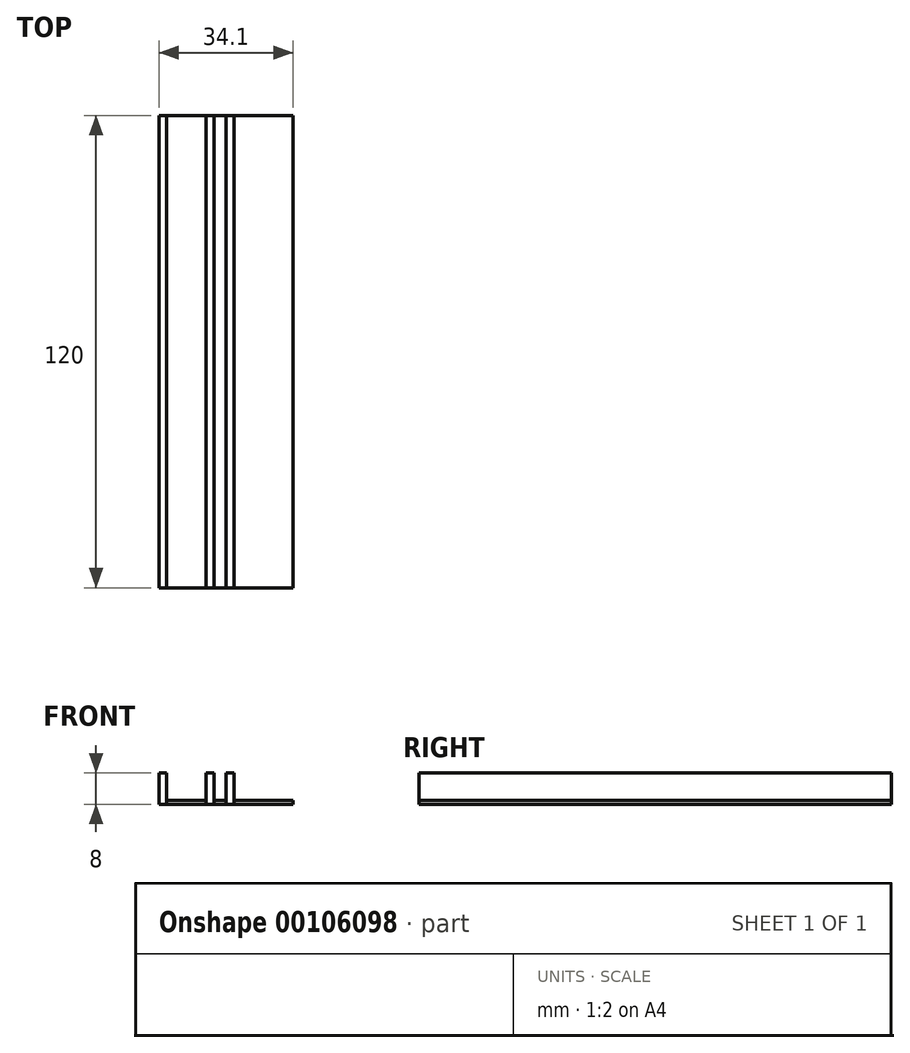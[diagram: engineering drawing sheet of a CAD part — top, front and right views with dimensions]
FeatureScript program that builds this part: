
annotation { "Feature Type Name" : "Feature", "Feature Type Description" : "" }
export const myFeature = defineFeature(function(context is Context, id is Id, definition is map)
    precondition{}
    {
        {
            var Q0;
            Q0=qCreatedBy(makeId("Top.planeOp"),FACE);
            var sketch = newSketch(context, id + "F0", { "sketchPlane" : qUnion([Q0])});
            skLineSegment(sketch, "E0.right", {"start": v(0, 44.94) * mm, "end": v(0, -75.06) * mm});
            skLineSegment(sketch, "E1", {"start": v(2, 44.94) * mm, "end": v(0, 44.94) * mm});
            skLineSegment(sketch, "E2", {"start": v(2, 44.94) * mm, "end": v(12, 44.94) * mm});
            skLineSegment(sketch, "E3.bottom", {"start": v(0, -75.06) * mm, "end": v(2, -75.06) * mm});
            skLineSegment(sketch, "E3.top", {"start": v(0, 44.94) * mm, "end": v(2, 44.94) * mm});
            skLineSegment(sketch, "E3.left", {"start": v(0, -75.06) * mm, "end": v(0, 44.94) * mm});
            skLineSegment(sketch, "E3.right", {"start": v(2, -75.06) * mm, "end": v(2, 44.94) * mm});
            skLineSegment(sketch, "E4.bottom", {"start": v(2, -75.06) * mm, "end": v(12, -75.06) * mm});
            skLineSegment(sketch, "E4.right", {"start": v(12, -75.06) * mm, "end": v(12, 44.94) * mm});
            skLineSegment(sketch, "E5", {"start": v(0, 44.94) * mm, "end": v(-3.1, 44.94) * mm});
            skLineSegment(sketch, "E6", {"start": v(-3.1, 44.94) * mm, "end": v(-5.1, 44.94) * mm});
            skLineSegment(sketch, "E7", {"start": v(-5.1, 44.94) * mm, "end": v(-20.1, 44.94) * mm});
            skLineSegment(sketch, "E8.bottom", {"start": v(-3.1, 44.94) * mm, "end": v(0, 44.94) * mm});
            skLineSegment(sketch, "E8.top", {"start": v(-3.1, -75.06) * mm, "end": v(0, -75.06) * mm});
            skLineSegment(sketch, "E8.left", {"start": v(-3.1, 44.94) * mm, "end": v(-3.1, -75.06) * mm});
            skLineSegment(sketch, "E9.bottom", {"start": v(-5.1, 44.94) * mm, "end": v(-3.1, 44.94) * mm});
            skLineSegment(sketch, "E9.top", {"start": v(-5.1, -75.06) * mm, "end": v(-3.1, -75.06) * mm});
            skLineSegment(sketch, "E9.left", {"start": v(-5.1, 44.94) * mm, "end": v(-5.1, -75.06) * mm});
            skLineSegment(sketch, "E10.bottom", {"start": v(-20.1, 44.94) * mm, "end": v(-5.1, 44.94) * mm});
            skLineSegment(sketch, "E10.top", {"start": v(-20.1, -75.06) * mm, "end": v(-5.1, -75.06) * mm});
            skLineSegment(sketch, "E10.left", {"start": v(-20.1, 44.94) * mm, "end": v(-20.1, -75.06) * mm});
            skLineSegment(sketch, "E11", {"start": v(12, 44.94) * mm, "end": v(14, 44.94) * mm});
            skLineSegment(sketch, "E12", {"start": v(14, 44.94) * mm, "end": v(14, -75.05) * mm});
            skLineSegment(sketch, "E13", {"start": v(14, -75.05) * mm, "end": v(12, -75.06) * mm});
            skLineSegment(sketch, "E14", {"start": v(14, 44.94) * mm, "end": v(17.1, 44.94) * mm});
            skLineSegment(sketch, "E15", {"start": v(17.1, 44.94) * mm, "end": v(17.1, -75.05) * mm});
            skLineSegment(sketch, "E16", {"start": v(17.1, -75.05) * mm, "end": v(14, -75.05) * mm});
            skLineSegment(sketch, "E17", {"start": v(17.1, 44.94) * mm, "end": v(19.1, 44.94) * mm});
            skLineSegment(sketch, "E18", {"start": v(19.1, 44.94) * mm, "end": v(19.1, -75.05) * mm});
            skLineSegment(sketch, "E19", {"start": v(19.1, -75.05) * mm, "end": v(17.1, -75.05) * mm});
            skLineSegment(sketch, "E20", {"start": v(19.1, 44.94) * mm, "end": v(34.1, 44.94) * mm});
            skLineSegment(sketch, "E21", {"start": v(34.1, 44.94) * mm, "end": v(34.1, -75.05) * mm});
            skLineSegment(sketch, "E22", {"start": v(34.1, -75.05) * mm, "end": v(19.1, -75.05) * mm});
            skSolve(sketch);
        }
        {
            var Q0;
            {var subQ3=sQuery(id+"F0.wireOp",EDGE,"E8.bottom");Q0=makeQuery(id+"F0.imprint","IMPRINT",FACE,{"disambiguationData":[TD([[makeQuery(id+"F0.imprint","IMPRINT",EDGE,{"derivedFrom":subQ3}),-1.0]])]});}
            var Q1;
            Q1=makeQuery(id+"F0.imprint","IMPRINT",FACE,{"disambiguationData":[TD([[makeQuery(id+"F0.imprint","IMPRINT",EDGE,{"derivedFrom":sQuery(id+"F0.wireOp",EDGE,"E4.bottom")}),1.0]])]});
            var Q2;
            Q2=makeQuery(id+"F0.imprint","IMPRINT",FACE,{"disambiguationData":[TD([[makeQuery(id+"F0.imprint","IMPRINT",EDGE,{"derivedFrom":sQuery(id+"F0.wireOp",EDGE,"E10.bottom")}),-1.0]])]});
            var Q3;
            Q3=makeQuery(id+"F0.imprint","IMPRINT",FACE,{"disambiguationData":[TD([[makeQuery(id+"F0.imprint","IMPRINT",EDGE,{"derivedFrom":sQuery(id+"F0.wireOp",EDGE,"E18")}),1.0]])]});
            var Q4;
            Q4=makeQuery(id+"F0.imprint","IMPRINT",FACE,{"disambiguationData":[TD([[makeQuery(id+"F0.imprint","IMPRINT",EDGE,{"derivedFrom":sQuery(id+"F0.wireOp",EDGE,"E12")}),1.0]])]});
            extrude(context, id + "F1", {"entities" : qUnion([Q0, Q1, Q2, Q3, Q4]), "depth" : 1 * mm});
        }
        {
            var Q0;
            Q0=makeQuery(id+"F0.imprint","IMPRINT",FACE,{"disambiguationData":[TD([[makeQuery(id+"F0.imprint","IMPRINT",EDGE,{"derivedFrom":sQuery(id+"F0.wireOp",EDGE,"E9.bottom")}),-1.0]])]});
            var Q1;
            {var subQ2=sQuery(id+"F0.wireOp",EDGE,"E3.bottom");Q1=makeQuery(id+"F0.imprint","IMPRINT",FACE,{"disambiguationData":[TD([[makeQuery(id+"F0.imprint","IMPRINT",EDGE,{"derivedFrom":subQ2}),1.0]])]});}
            var Q2;
            Q2=makeQuery(id+"F0.imprint","IMPRINT",FACE,{"disambiguationData":[TD([[makeQuery(id+"F0.imprint","IMPRINT",EDGE,{"derivedFrom":sQuery(id+"F0.wireOp",EDGE,"E4.right")}),-1.0]])]});
            var Q3;
            Q3=makeQuery(id+"F0.imprint","IMPRINT",FACE,{"disambiguationData":[TD([[makeQuery(id+"F0.imprint","IMPRINT",EDGE,{"derivedFrom":sQuery(id+"F0.wireOp",EDGE,"E15")}),1.0]])]});
            extrude(context, id + "F2", {"entities" : qUnion([Q0, Q1, Q2, Q3]), "depth" : 8 * mm});
        }
        {
            var Q0;
            Q0=makeQuery(id+"F2.opExtrude","SWEPT_FACE",FACE,{"disambiguationData":[OSD([sQuery(id+"F0.wireOp",EDGE,"E3.right")])]});
            var sketch = newSketch(context, id + "F3", { "sketchPlane" : qUnion([Q0])});
            skLineSegment(sketch, "E23.bottom", {"start": v(44.94, 8) * mm, "end": v(43.94, 8) * mm});
            skLineSegment(sketch, "E23.top", {"start": v(44.94, 1) * mm, "end": v(43.94, 1) * mm});
            skLineSegment(sketch, "E23.left", {"start": v(44.94, 8) * mm, "end": v(44.94, 1) * mm});
            skLineSegment(sketch, "E23.right", {"start": v(43.94, 8) * mm, "end": v(43.94, 1) * mm});
            skSolve(sketch);
        }
    });
